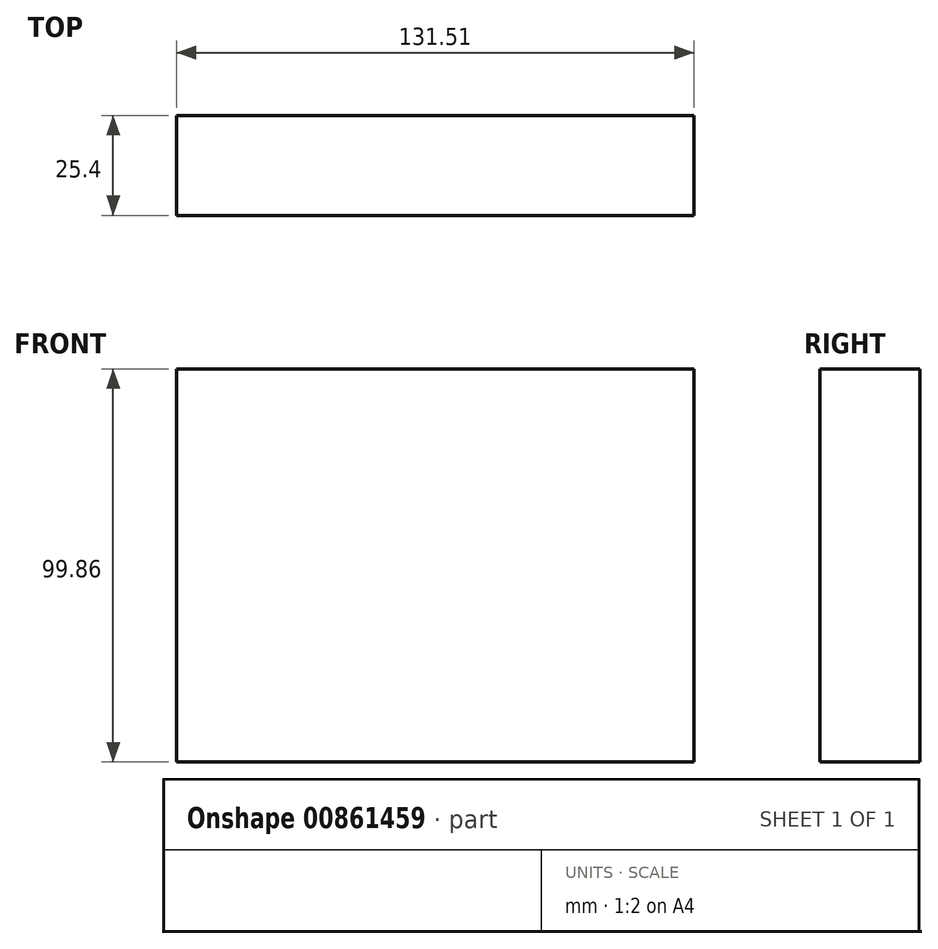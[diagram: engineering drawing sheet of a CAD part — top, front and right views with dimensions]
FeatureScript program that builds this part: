
annotation { "Feature Type Name" : "Feature", "Feature Type Description" : "" }
export const myFeature = defineFeature(function(context is Context, id is Id, definition is map)
    precondition{}
    {
        {
            var Q0;
            Q0=qCreatedBy(makeId("Front.planeOp"),FACE);
            var sketch = newSketch(context, id + "F0", { "sketchPlane" : qUnion([Q0])});
            skLineSegment(sketch, "E0.bottom", {"start": v(-222.33, 99.86) * mm, "end": v(-90.82, 99.86) * mm});
            skLineSegment(sketch, "E0.top", {"start": v(-222.33, 0) * mm, "end": v(-90.82, 0) * mm});
            skLineSegment(sketch, "E0.left", {"start": v(-222.33, 99.86) * mm, "end": v(-222.33, 0) * mm});
            skLineSegment(sketch, "E0.right", {"start": v(-90.82, 99.86) * mm, "end": v(-90.82, 0) * mm});
            skSolve(sketch);
        }
        {
            var Q0;
            Q0=makeQuery(id+"F0.imprint","IMPRINT",FACE,{"disambiguationData":[TD([[makeQuery(id+"F0.imprint","IMPRINT",EDGE,{"derivedFrom":sQuery(id+"F0.wireOp",EDGE,"E0.bottom")}),-1.0]])]});
            extrude(context, id + "F1", {"entities" : qUnion([Q0]), "depth" : 25.4 * mm, "offsetDistance" : 25.4 * mm});
        }
    });
